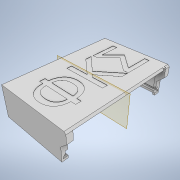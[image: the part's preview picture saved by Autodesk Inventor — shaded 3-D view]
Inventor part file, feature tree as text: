
AUTODESK INVENTOR PART (.ipt)
format: ipt  version: 2020.1 (Build 241239000, 239)  size: 387,584 bytes
history: native  units: mm
features: extrude x12, sketch x12, mirror x3, projected_geometry x3, chamfer x2, plane x1
ambient origin geometry x8: Origin, YZ Plane, XZ Plane, XY Plane, X Axis, Y Axis, Z Axis, Center Point
bodies: Solid1 (feature_tree)
feature tree (33):
  extrude  "Extrusion1"  Depth=100.0mm
  extrude  "Extrusion2"  Depth=3.0mm
  extrude  "Extrusion3"  Depth=20.868mm
  plane  "Work Plane1"
  mirror  "Mirror1"
  extrude  "Extrusion5"  TaperAngle=135.0deg  [1 undecoded]
  extrude  "Extrusion6"  TaperAngle=0.0deg  [1 undecoded]
  mirror  "Mirror3"
  extrude  "Extrusion8"  Depth=5.419mm
  chamfer  "Chamfer1"  Distance=2.0mm
  extrude  "Extrusion9"  Depth=3.0mm
  chamfer  "Chamfer4"  Distance=0.25mm
  extrude  "Extrusion10"  Depth=5.418mm
  extrude  "Extrusion11"  Depth=1.5mm
  extrude  "Extrusion12"  Depth=1.5mm TaperAngle=0.0deg
  mirror  "Mirror4"
  extrude  "Extrusion13"  Depth=5.418mm TaperAngle=45.0deg
  extrude  "Extrusion14"  TaperAngle=90.0deg  [1 undecoded]
  sketch  "Sketch1"  dims[d0=63.837mm d1=100.0mm]
  sketch  "Sketch2"  dims[d2=1.5mm d3=0.0mm d4=3.0mm]
  sketch  "Sketch3"  dims[d5=25.0mm d6=0.0mm d7=20.868mm]
  sketch  "Sketch7"  dims[d8=2.828427mm d9=135.0deg]
  projected_geometry  "Projected Loop2"
  projected_geometry  "Projected Loop3"
  sketch  "Sketch8"  dims[d10=1.0mm d11=0.0mm d12=0.0mm]
  sketch  "Sketch10"  dims[d22=1.0mm d23=0.0mm d24=5.419mm]
  sketch  "Sketch11"  dims[d26=0.0mm d27=2.0mm d28=0.0mm]
  sketch  "Sketch12"  dims[d31=3.0mm d32=0.0mm d33=15.0mm]
  projected_geometry  "Projected Loop5"
  sketch  "Sketch13"  dims[d34=15.0mm]
  sketch  "Sketch14"  dims[d35=30.0mm]
  sketch  "Sketch15"  dims[d36=30.0mm d37=0.25mm d38=0.0mm]
  sketch  "Sketch16"  dims[d39=1.5mm d40=2.0mm d41=45.0deg d48=5.418mm d49=13.0mm d50=10.0mm d51=0.0mm d52=5.418mm d53=2.0mm d54=45.0deg d55=90.0deg d56=2.0mm d57=0.0mm d58=2.0mm d60=2.0mm d61=0.0mm d62=2.25mm d63=10.0mm d64=0.0mm d65=10.0mm d66=0.0mm d67=2.0mm d68=5.0mm d69=1.5mm d70=0.0mm]
note: 3 required parameter values undecoded (feature->parameter linkage not recoverable at this tier; creation-order binding heuristic only, values carry confidence <= 0.55)
